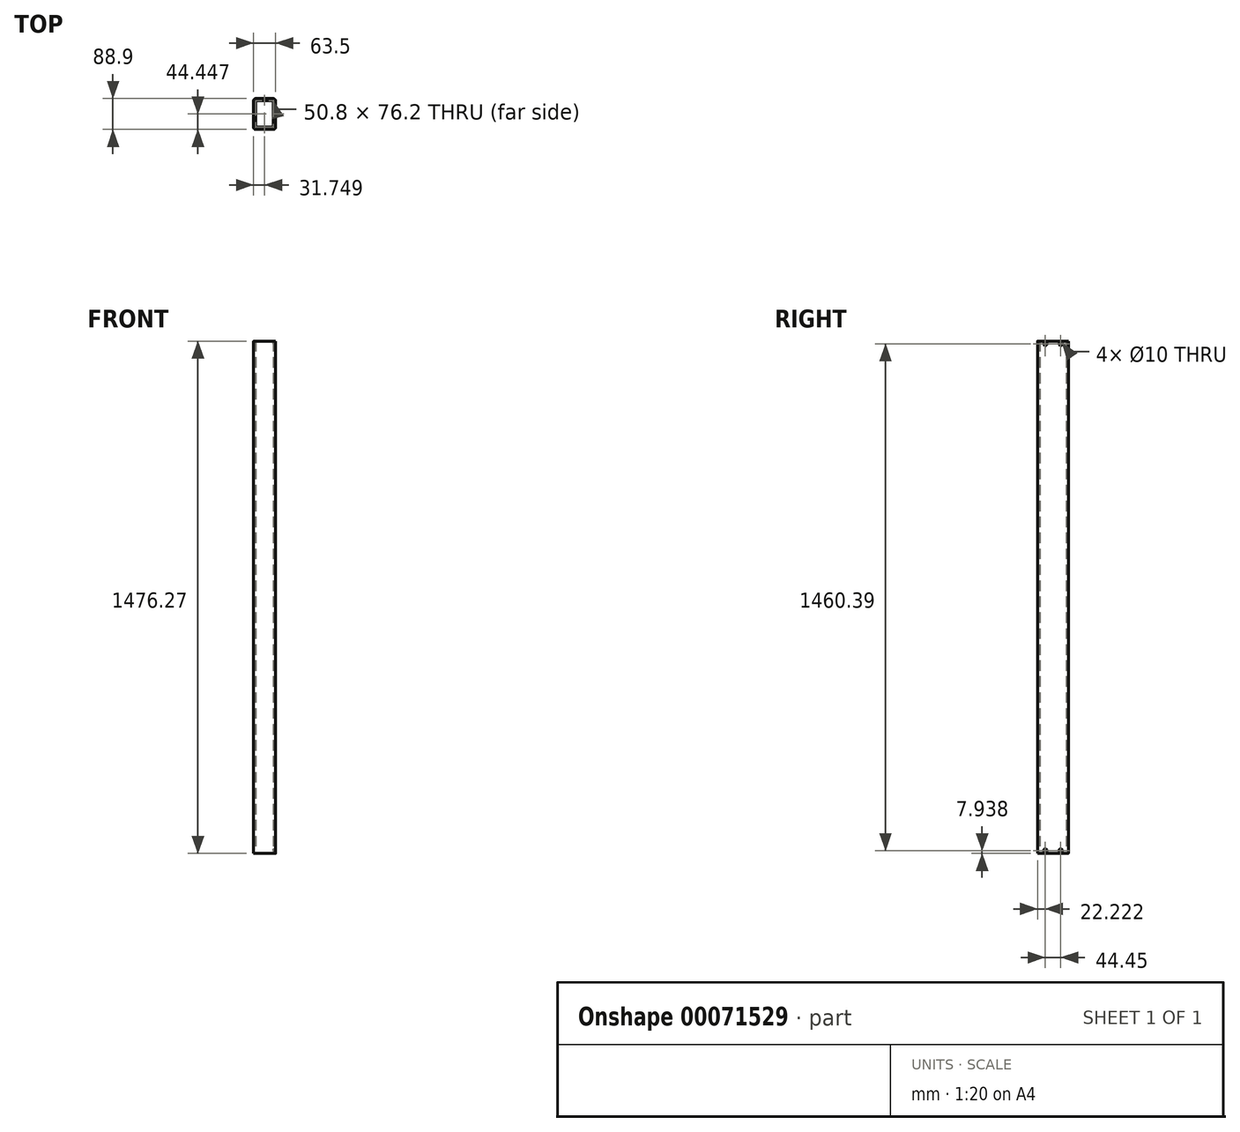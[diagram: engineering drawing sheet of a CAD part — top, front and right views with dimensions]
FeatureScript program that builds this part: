
annotation { "Feature Type Name" : "Feature", "Feature Type Description" : "" }
export const myFeature = defineFeature(function(context is Context, id is Id, definition is map)
    precondition{}
    {
        {
            var Q0;
            Q0=qCreatedBy(makeId("Top.planeOp"),FACE);
            var sketch = newSketch(context, id + "F0", { "sketchPlane" : qUnion([Q0])});
            skLineSegment(sketch, "E0.bottom", {"start": v(-23.83, -61.81) * mm, "end": v(26.97, -61.81) * mm});
            skLineSegment(sketch, "E0.top", {"start": v(-23.83, 27.09) * mm, "end": v(26.97, 27.09) * mm});
            skLineSegment(sketch, "E0.left", {"start": v(-30.18, -55.46) * mm, "end": v(-30.18, 20.74) * mm});
            skLineSegment(sketch, "E0.right", {"start": v(33.32, -55.46) * mm, "end": v(33.32, 20.74) * mm});
            skPoint(sketch, "E1.visualSharp", {"position": v(-30.18, 27.09) * mm});
            skArc(sketch, "E1.filletArc", {"start": v(-23.83, 27.09) * mm, "mid": v(-28.32, 25.23) * mm, "end": v(-30.18, 20.74) * mm});
            skPoint(sketch, "E2.visualSharp", {"position": v(33.32, 27.09) * mm});
            skArc(sketch, "E2.filletArc", {"start": v(33.32, 20.74) * mm, "mid": v(31.46, 25.23) * mm, "end": v(26.97, 27.09) * mm});
            skPoint(sketch, "E3.visualSharp", {"position": v(33.32, -61.81) * mm});
            skArc(sketch, "E3.filletArc", {"start": v(26.97, -61.81) * mm, "mid": v(31.46, -59.95) * mm, "end": v(33.32, -55.46) * mm});
            skPoint(sketch, "E4.visualSharp", {"position": v(-30.18, -61.81) * mm});
            skArc(sketch, "E4.filletArc", {"start": v(-30.18, -55.46) * mm, "mid": v(-28.32, -59.95) * mm, "end": v(-23.83, -61.81) * mm});
            skLineSegment(sketch, "E5.bottom", {"start": v(-23.83, -55.46) * mm, "end": v(26.97, -55.46) * mm});
            skLineSegment(sketch, "E5.top", {"start": v(-23.83, 20.74) * mm, "end": v(26.97, 20.74) * mm});
            skLineSegment(sketch, "E5.left", {"start": v(-23.83, -55.46) * mm, "end": v(-23.83, 20.74) * mm});
            skLineSegment(sketch, "E5.right", {"start": v(26.97, -55.46) * mm, "end": v(26.97, 20.74) * mm});
            skSolve(sketch);
        }
        {
            var Q0;
            Q0=makeQuery(id+"F0.imprint","IMPRINT",FACE,{"disambiguationData":[TD([[makeQuery(id+"F0.imprint","IMPRINT",EDGE,{"derivedFrom":sQuery(id+"F0.wireOp",EDGE,"E0.bottom")}),1.0]])]});
            extrude(context, id + "F1", {"entities" : qUnion([Q0]), "depth" : 1476.27 * mm});
        }
        {
            var Q0;
            Q0=makeQuery(id+"F1.opExtrude","SWEPT_FACE",FACE,{"disambiguationData":[OSD([sQuery(id+"F0.wireOp",EDGE,"E0.right")])]});
            var sketch = newSketch(context, id + "F2", { "sketchPlane" : qUnion([Q0])});
            skCircle(sketch, "E6", {"center": v(4.86, 7.94) * mm, "radius": 5 * mm});
            skCircle(sketch, "E7", {"center": v(-39.59, 7.94) * mm, "radius": 5 * mm});
            skCircle(sketch, "E8", {"center": v(4.86, 1468.33) * mm, "radius": 5 * mm});
            skCircle(sketch, "E9", {"center": v(-39.59, 1468.33) * mm, "radius": 5 * mm});
            skSolve(sketch);
        }
        {
            var Q0;
            Q0=qSketchRegion(id+"F2",true);
            extrude(context, id + "F3", {"entities" : qUnion([Q0]), "operationType" : NewBodyOperationType.REMOVE, "oppositeDirection" : true, "depth" : 15.32 * mm});
        }
    });
